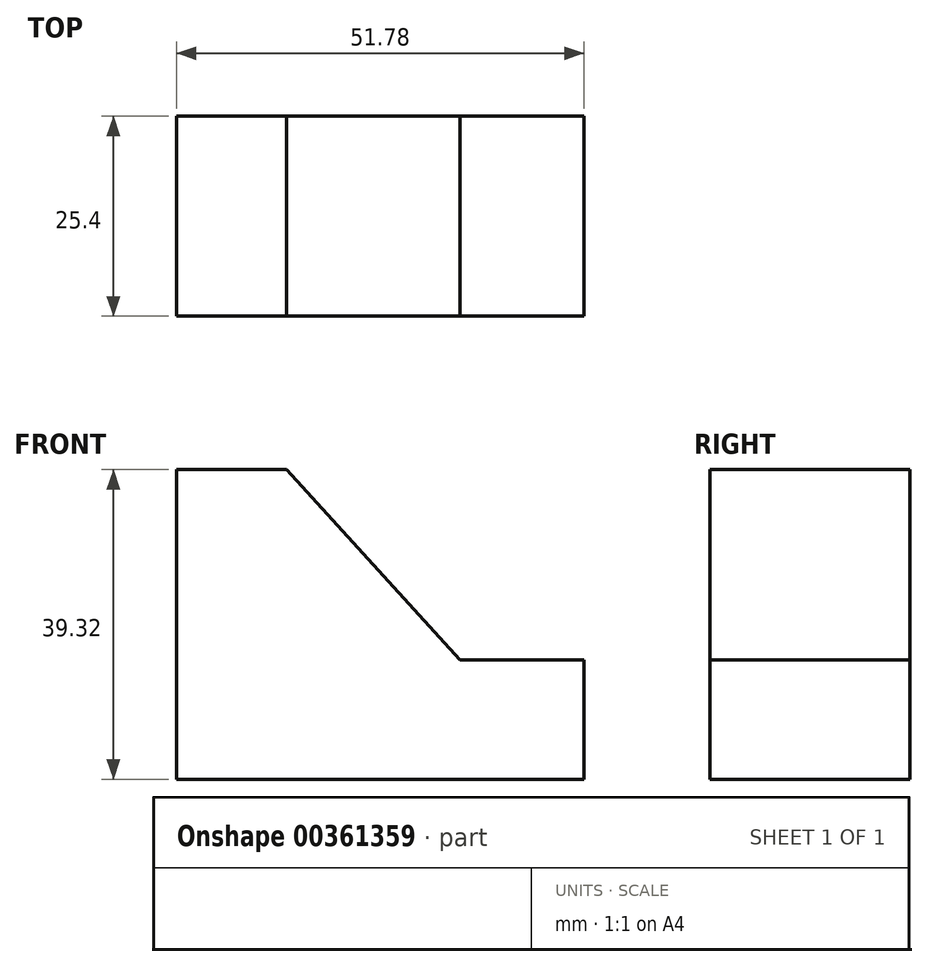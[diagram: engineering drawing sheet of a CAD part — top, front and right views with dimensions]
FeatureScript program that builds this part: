
annotation { "Feature Type Name" : "Feature", "Feature Type Description" : "" }
export const myFeature = defineFeature(function(context is Context, id is Id, definition is map)
    precondition{}
    {
        {
            var Q0;
            Q0=qCreatedBy(makeId("Front.planeOp"),FACE);
            var sketch = newSketch(context, id + "F0", { "sketchPlane" : qUnion([Q0])});
            skLineSegment(sketch, "E0", {"start": v(0, 0) * mm, "end": v(0, 39.32) * mm});
            skLineSegment(sketch, "E1", {"start": v(0, 39.32) * mm, "end": v(14.02, 39.32) * mm});
            skLineSegment(sketch, "E2", {"start": v(14.02, 39.32) * mm, "end": v(36.01, 15.18) * mm});
            skLineSegment(sketch, "E3", {"start": v(36.01, 15.18) * mm, "end": v(51.78, 15.18) * mm});
            skLineSegment(sketch, "E4", {"start": v(51.78, 15.18) * mm, "end": v(51.78, 0) * mm});
            skLineSegment(sketch, "E5", {"start": v(0, 0) * mm, "end": v(51.78, 0) * mm});
            skSolve(sketch);
        }
        {
            var Q0;
            Q0 = qSketchRegion(id + "F0", true);
            extrude(context, id + "F1", {"entities" : qUnion([Q0]), "depth" : 25.4 * mm});
        }
    });
